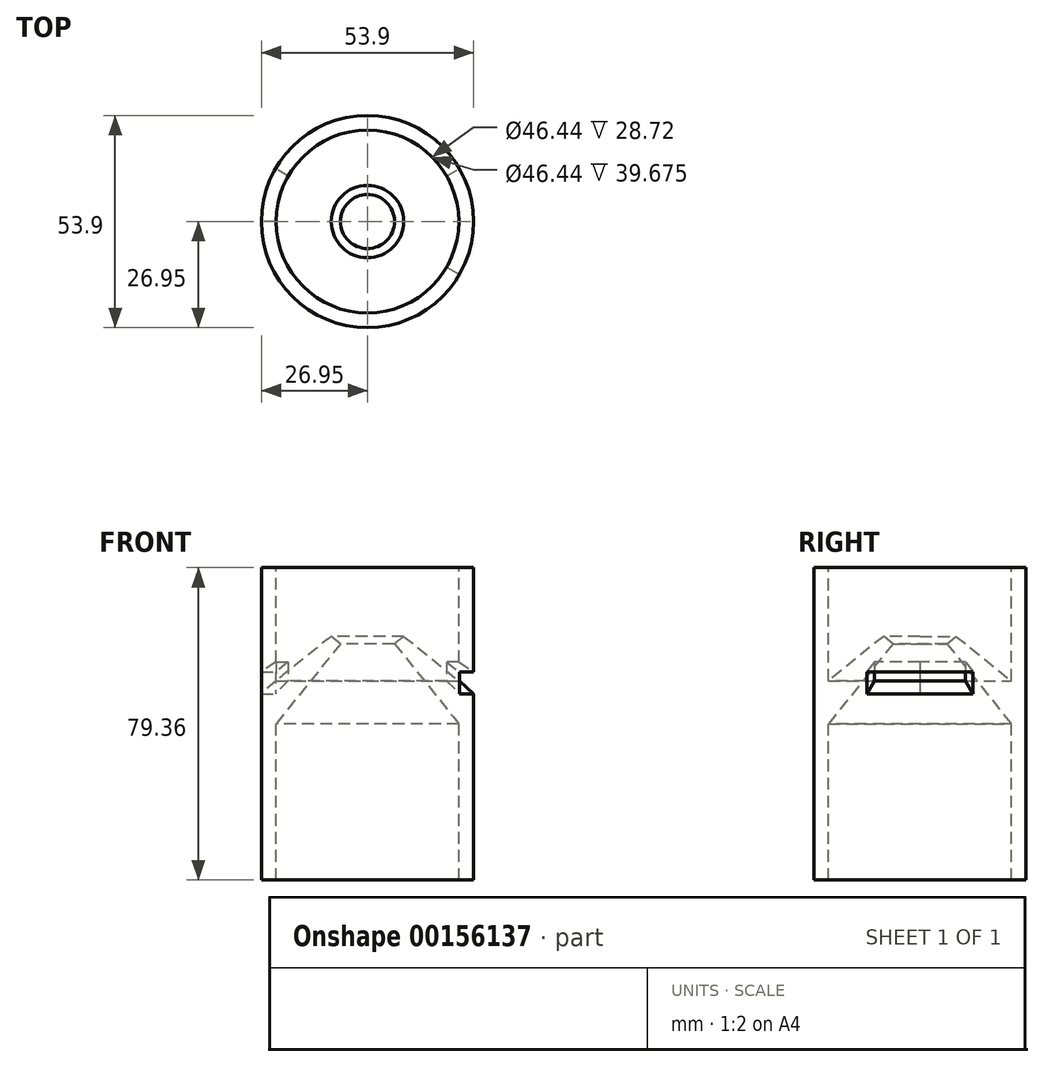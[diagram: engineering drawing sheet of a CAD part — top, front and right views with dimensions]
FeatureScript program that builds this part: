
annotation { "Feature Type Name" : "Feature", "Feature Type Description" : "" }
export const myFeature = defineFeature(function(context is Context, id is Id, definition is map)
    precondition{}
    {
        {
            var Q0;
            Q0=qCreatedBy(makeId("Front.planeOp"),FACE);
            var sketch = newSketch(context, id + "F0", { "sketchPlane" : qUnion([Q0])});
            skLineSegment(sketch, "E0", {"start": v(26.95, 39.68) * mm, "end": v(26.95, -39.68) * mm});
            skLineSegment(sketch, "E1", {"start": v(23.22, 39.68) * mm, "end": v(23.22, 10.96) * mm});
            skLineSegment(sketch, "E2", {"start": v(23.22, -39.68) * mm, "end": v(26.95, -39.68) * mm});
            skLineSegment(sketch, "E3", {"start": v(26.95, 39.68) * mm, "end": v(23.22, 39.68) * mm});
            skLineSegment(sketch, "E4", {"start": v(23.22, 0) * mm, "end": v(6.86, 20.37) * mm});
            skLineSegment(sketch, "E5", {"start": v(6.86, 20.37) * mm, "end": v(9.2, 22.25) * mm});
            skLineSegment(sketch, "E6", {"start": v(9.2, 22.25) * mm, "end": v(23.22, 10.96) * mm});
            skLineSegment(sketch, "E7.trimOffspring", {"start": v(23.22, 0) * mm, "end": v(23.22, -39.68) * mm});
            skLineSegment(sketch, "E8", {"start": v(0, 43.18) * mm, "end": v(0, -32.27) * mm});
            skLineSegment(sketch, "E9", {"start": v(23.22, 10.96) * mm, "end": v(26.95, 7.65) * mm});
            skLineSegment(sketch, "E10", {"start": v(23.22, 15.71) * mm, "end": v(26.95, 13.23) * mm});
            skSolve(sketch);
        }
        {
            var Q0;
            Q0=qSketchRegion(id+"F0",true);
            var Q1;
            Q1=sQuery(id+"F0.wireOp",EDGE,"E8");
            revolve(context, id + "F1", {"entities" : qUnion([Q0]), "axis" : qUnion([Q1]), "revolveType" : RevolveType.FULL});
        }
        {
            var Q0;
            {var subQ0=sQuery(id+"F0.wireOp",EDGE,"E9");Q0=makeQuery(id+"F0.imprint","IMPRINT",FACE,{"disambiguationData":[TD([[makeQuery(id+"F0.imprint","IMPRINT",EDGE,{"derivedFrom":subQ0}),1.0]])]});}
            var Q1;
            Q1=sQuery(id+"F0.wireOp",EDGE,"E8");
            revolve(context, id + "F2", {"operationType" : NewBodyOperationType.REMOVE, "entities" : qUnion([Q0]), "axis" : qUnion([Q1]), "revolveType" : RevolveType.TWO_DIRECTIONS, "oppositeDirection" : true, "angle" : 30 * degree, "angleBack" : 330 * degree});
        }
        {
            var Q0;
            {var subQ0=sQuery(id+"F0.wireOp",EDGE,"E9");Q0=makeQuery(id+"F0.imprint","IMPRINT",FACE,{"disambiguationData":[TD([[makeQuery(id+"F0.imprint","IMPRINT",EDGE,{"derivedFrom":subQ0}),1.0]])]});}
            var Q1;
            Q1=sQuery(id+"F0.wireOp",EDGE,"E8");
            revolve(context, id + "F3", {"operationType" : NewBodyOperationType.REMOVE, "entities" : qUnion([Q0]), "axis" : qUnion([Q1]), "revolveType" : RevolveType.TWO_DIRECTIONS, "oppositeDirection" : true, "angle" : 180 * degree, "angleBack" : 150 * degree});
        }
    });
